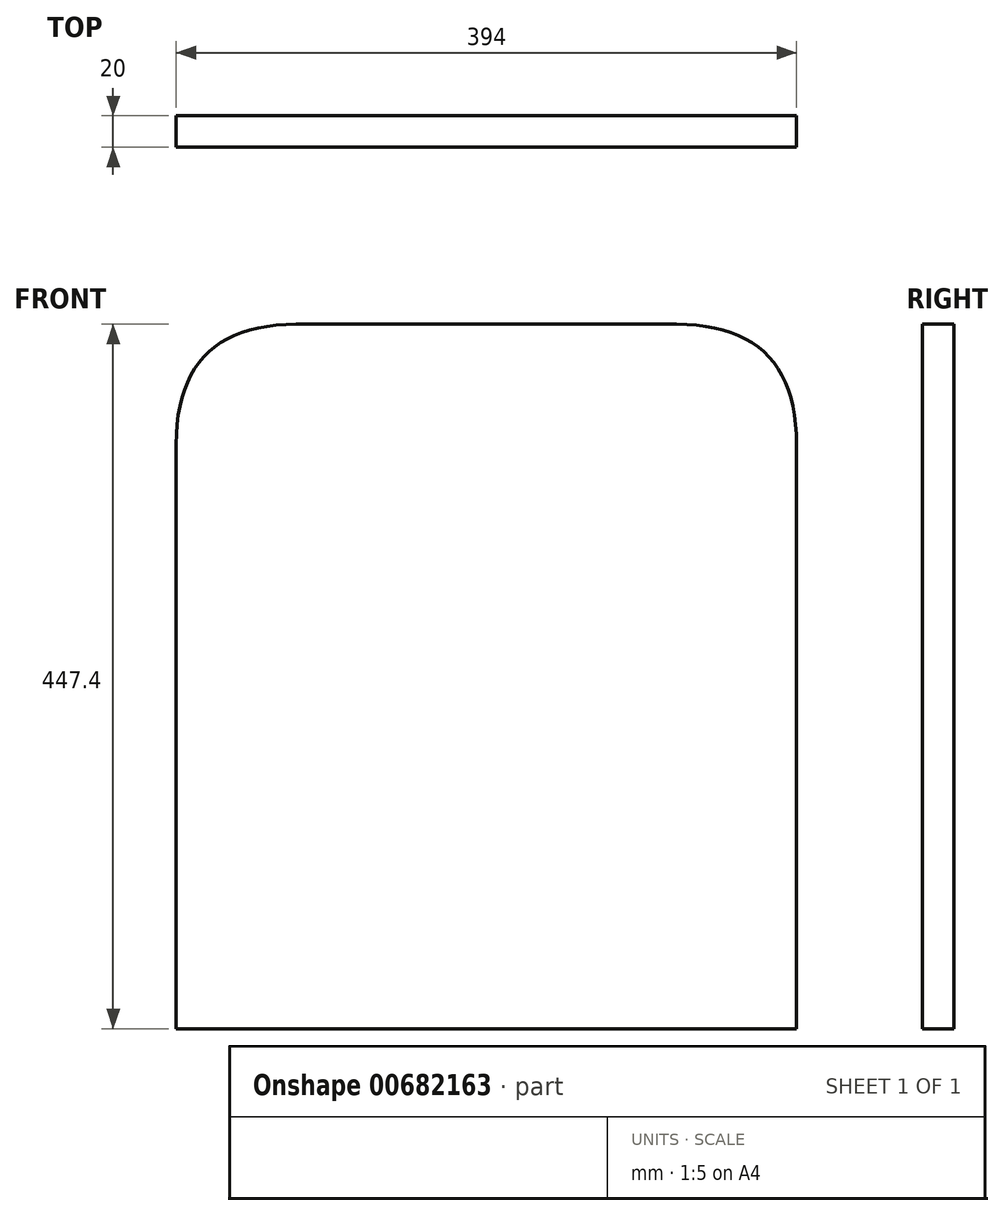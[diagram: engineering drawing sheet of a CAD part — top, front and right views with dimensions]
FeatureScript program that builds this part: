
annotation { "Feature Type Name" : "Feature", "Feature Type Description" : "" }
export const myFeature = defineFeature(function(context is Context, id is Id, definition is map)
    precondition{}
    {
        {
            var Q0;
            Q0=qCreatedBy(makeId("Front.planeOp"),FACE);
            var sketch = newSketch(context, id + "F0", { "sketchPlane" : qUnion([Q0])});
            skLineSegment(sketch, "E0.bottom", {"start": v(-163.8, 266.54) * mm, "end": v(230.2, 266.54) * mm});
            skLineSegment(sketch, "E0.top", {"start": v(-163.8, -180.86) * mm, "end": v(230.2, -180.86) * mm});
            skLineSegment(sketch, "E0.left", {"start": v(-163.8, 266.54) * mm, "end": v(-163.8, -180.86) * mm});
            skLineSegment(sketch, "E0.right", {"start": v(230.2, 266.54) * mm, "end": v(230.2, -180.86) * mm});
            skSolve(sketch);
        }
        {
            var Q0;
            Q0=makeQuery(id+"F0.imprint","IMPRINT",FACE,{"disambiguationData":[TD([[makeQuery(id+"F0.imprint","IMPRINT",EDGE,{"derivedFrom":sQuery(id+"F0.wireOp",EDGE,"E0.bottom")}),-1.0]])]});
            extrude(context, id + "F1", {"entities" : qUnion([Q0]), "depth" : 20 * mm, "offsetDistance" : 25.4 * mm});
        }
        {
            var Q0;
            Q0=makeQuery(id+"F1.opExtrude","SWEPT_EDGE",EDGE,{"disambiguationData":[OSD([sQuery(id+"F0.wireOp",EDGE,"E0.bottom"),sQuery(id+"F0.wireOp",EDGE,"E0.right")])]});
            var Q1;
            Q1=makeQuery(id+"F1.opExtrude","SWEPT_EDGE",EDGE,{"disambiguationData":[OSD([sQuery(id+"F0.wireOp",EDGE,"E0.bottom"),sQuery(id+"F0.wireOp",EDGE,"E0.left")])]});
            fillet(context, id + "F2", {"entities" : qUnion([Q0, Q1]), "radius" : 76.2 * mm, "tangentPropagation" : true, "rho" : 0.5, "crossSection" : FilletCrossSection.CONIC, "allowEdgeOverflow" : false});
        }
    });
